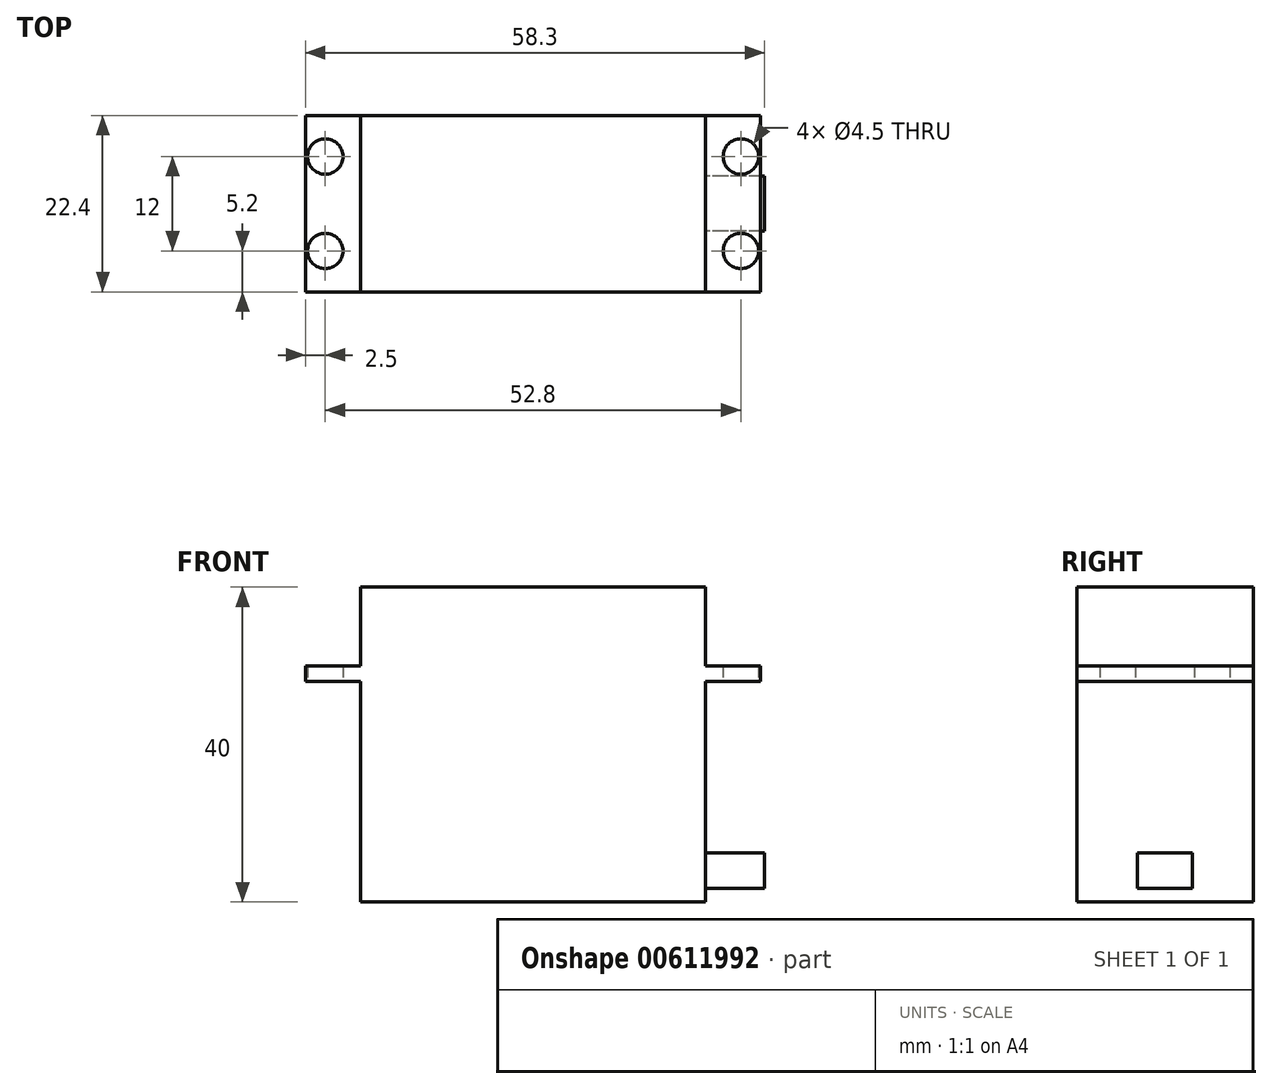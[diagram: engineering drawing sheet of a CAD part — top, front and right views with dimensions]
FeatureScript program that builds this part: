
annotation { "Feature Type Name" : "Feature", "Feature Type Description" : "" }
export const myFeature = defineFeature(function(context is Context, id is Id, definition is map)
    precondition{}
    {
        {
            var Q0;
            Q0=qCreatedBy(makeId("Top.planeOp"),FACE);
            var sketch = newSketch(context, id + "F0", { "sketchPlane" : qUnion([Q0])});
            skLineSegment(sketch, "E0.bottom", {"start": v(21.9, -11.2) * mm, "end": v(-21.9, -11.2) * mm});
            skLineSegment(sketch, "E0.top", {"start": v(21.9, 11.2) * mm, "end": v(-21.9, 11.2) * mm});
            skLineSegment(sketch, "E0.left", {"start": v(21.9, -11.2) * mm, "end": v(21.9, 11.2) * mm});
            skLineSegment(sketch, "E0.right", {"start": v(-21.9, -11.2) * mm, "end": v(-21.9, 11.2) * mm});
            skPoint(sketch, "E0.middle", {"position": v(0, 0) * mm});
            skLineSegment(sketch, "E1.bottom", {"start": v(-21.9, 11.2) * mm, "end": v(0, 11.2) * mm});
            skLineSegment(sketch, "E1.top", {"start": v(-21.9, -11.2) * mm, "end": v(0, -11.2) * mm});
            skLineSegment(sketch, "E1.left", {"start": v(-21.9, 11.2) * mm, "end": v(-21.9, -11.2) * mm});
            skLineSegment(sketch, "E1.right", {"start": v(0, 11.2) * mm, "end": v(0, -11.2) * mm});
            skLineSegment(sketch, "E2.bottom", {"start": v(28.9, -11.2) * mm, "end": v(-28.9, -11.2) * mm});
            skLineSegment(sketch, "E2.top", {"start": v(28.9, 11.2) * mm, "end": v(-28.9, 11.2) * mm});
            skLineSegment(sketch, "E2.left", {"start": v(28.9, -11.2) * mm, "end": v(28.9, 11.2) * mm});
            skLineSegment(sketch, "E2.right", {"start": v(-28.9, -11.2) * mm, "end": v(-28.9, 11.2) * mm});
            skLineSegment(sketch, "E3.bottom", {"start": v(26.4, -6) * mm, "end": v(-26.4, -6) * mm, "construction": true});
            skLineSegment(sketch, "E3.top", {"start": v(26.4, 6) * mm, "end": v(-26.4, 6) * mm, "construction": true});
            skLineSegment(sketch, "E3.left", {"start": v(26.4, -6) * mm, "end": v(26.4, 6) * mm, "construction": true});
            skLineSegment(sketch, "E3.right", {"start": v(-26.4, -6) * mm, "end": v(-26.4, 6) * mm, "construction": true});
            skLineSegment(sketch, "E4", {"start": v(26.4, 0) * mm, "end": v(10.7, 0) * mm, "construction": true});
            skPoint(sketch, "E4.endSnap0", {"position": v(26.4, 0) * mm});
            skSolve(sketch);
        }
        {
            var Q0;
            {var subQ0=sQuery(id+"F0.wireOp",EDGE,"E0.left");Q0=makeQuery(id+"F0.imprint","IMPRINT",FACE,{"disambiguationData":[TD([[makeQuery(id+"F0.imprint","IMPRINT",EDGE,{"derivedFrom":subQ0}),1.0]])]});}
            extrude(context, id + "F1", {"entities" : qUnion([Q0]), "depth" : 40 * mm, "offsetDistance" : 25 * mm});
        }
        {
            var Q0;
            {var subQ0=sQuery(id+"F0.wireOp",EDGE,"E0.left");Q0=makeQuery(id+"F0.imprint","IMPRINT",FACE,{"disambiguationData":[TD([[makeQuery(id+"F0.imprint","IMPRINT",EDGE,{"derivedFrom":subQ0}),-1.0]])]});}
            extrude(context, id + "F2", {"entities" : qUnion([Q0]), "operationType" : NewBodyOperationType.ADD, "depth" : 30 * mm, "offsetDistance" : 25 * mm, "hasSecondDirection" : true, "secondDirectionOppositeDirection" : false, "secondDirectionDepth" : 28 * mm});
        }
        {
            var Q0;
            Q0=sQuery(id+"F0.wireOp",VERTEX,"E3.bottom.start");
            var Q1;
            Q1=sQuery(id+"F0.wireOp",VERTEX,"E3.left.end");
            var Q2;
            Q2=makeQuery(id+"F1.opExtrude","SWEPT_BODY",BODY,{"disambiguationData":[OSD([sQuery(id+"F0.wireOp",EDGE,"E0.left"),sQuery(id+"F0.wireOp",EDGE,"E1.right"),sQuery(id+"F0.wireOp",EDGE,"E2.bottom"),sQuery(id+"F0.wireOp",EDGE,"E2.top")])]});
            hole(context, id + "F3", {"style" : HoleStyle.SIMPLE, "endStyle" : HoleEndStyle.THROUGH, "oppositeDirection" : true, "holeDiameter" : 4.5 * mm, "majorDiameter" : 5 * mm, "isTappedThrough" : true, "tappedDepth" : 12 * mm, "tapClearance" : 3, "locations" : qUnion([Q0, Q1]), "scope" : qUnion([Q2])});
        }
        {
            var Q0;
            Q0=makeQuery(id+"F1.opExtrude","SWEPT_BODY",BODY,{"disambiguationData":[OSD([sQuery(id+"F0.wireOp",EDGE,"E0.left"),sQuery(id+"F0.wireOp",EDGE,"E1.right"),sQuery(id+"F0.wireOp",EDGE,"E2.bottom"),sQuery(id+"F0.wireOp",EDGE,"E2.top")])]});
            var Q1;
            Q1=makeQuery(id+"F1.opExtrude","SWEPT_FACE",FACE,{"disambiguationData":[OSD([sQuery(id+"F0.wireOp",EDGE,"E1.right")])]});
            mirror(context, id + "F4", {"operationType" : NewBodyOperationType.ADD, "entities" : qUnion([Q0]), "mirrorPlane" : qUnion([Q1])});
        }
        {
            var Q0;
            {var subQ0=sQuery(id+"F0.wireOp",EDGE,"E2.top");var subQ1=sQuery(id+"F0.wireOp",EDGE,"E2.bottom");var subQ2=sQuery(id+"F0.wireOp",EDGE,"E0.left");Q0=makeQuery(id+"F2.boolean.opBoolean","SPLIT",FACE,{"disambiguationData":[TD([makeQuery(id+"F1.opExtrude","CAP_FACE",FACE,{"disambiguationData":[OSD([subQ2,sQuery(id+"F0.wireOp",EDGE,"E1.right"),subQ1,subQ0])],"isStart":true})])],"derivedFrom":makeQuery(id+"F1.opExtrude","SWEPT_FACE",FACE,{"disambiguationData":[OSD([subQ2])]})});}
            var sketch = newSketch(context, id + "F5", { "sketchPlane" : qUnion([Q0])});
            skLineSegment(sketch, "E5", {"start": v(0, 0) * mm, "end": v(0, 4) * mm, "construction": true});
            skPoint(sketch, "E5.endSnap0", {"position": v(0, 0) * mm});
            skLineSegment(sketch, "E6.bottom", {"start": v(3.5, 1.75) * mm, "end": v(-3.5, 1.75) * mm});
            skLineSegment(sketch, "E6.top", {"start": v(3.5, 6.25) * mm, "end": v(-3.5, 6.25) * mm});
            skLineSegment(sketch, "E6.left", {"start": v(3.5, 1.75) * mm, "end": v(3.5, 6.25) * mm});
            skLineSegment(sketch, "E6.right", {"start": v(-3.5, 1.75) * mm, "end": v(-3.5, 6.25) * mm});
            skPoint(sketch, "E6.middle", {"position": v(0, 4) * mm});
            skSolve(sketch);
        }
        {
            var Q0;
            Q0=makeQuery(id+"F5.imprint","IMPRINT",FACE,{"disambiguationData":[TD([[makeQuery(id+"F5.imprint","IMPRINT",EDGE,{"derivedFrom":sQuery(id+"F5.wireOp",EDGE,"E6.bottom")}),-1.0]])]});
            extrude(context, id + "F6", {"entities" : qUnion([Q0]), "operationType" : NewBodyOperationType.ADD, "depth" : 7.5 * mm, "offsetDistance" : 25 * mm});
        }
    });
